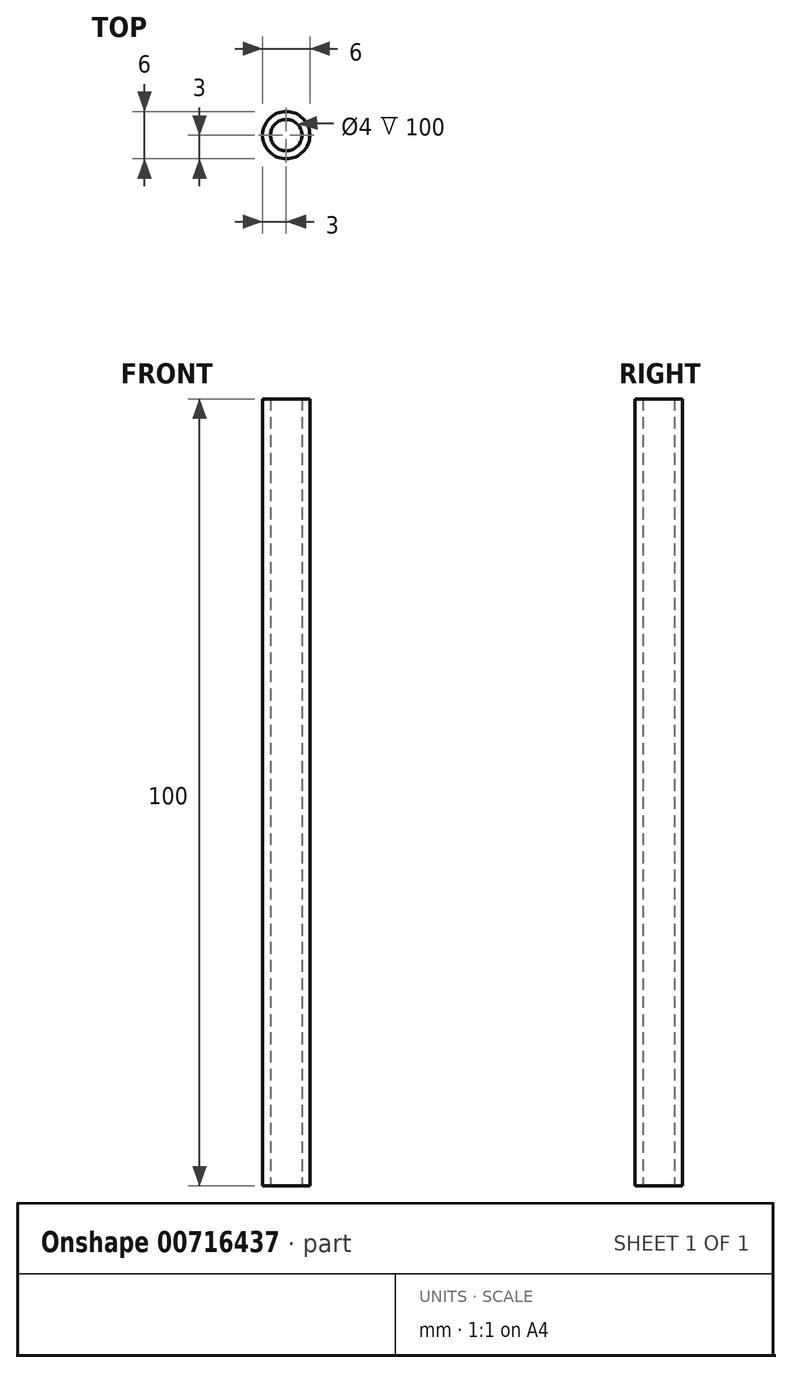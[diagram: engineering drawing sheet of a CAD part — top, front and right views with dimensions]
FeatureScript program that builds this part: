
annotation { "Feature Type Name" : "Feature", "Feature Type Description" : "" }
export const myFeature = defineFeature(function(context is Context, id is Id, definition is map)
    precondition{}
    {
        {
            var Q0;
            Q0=qCreatedBy(makeId("Top.planeOp"),FACE);
            var sketch = newSketch(context, id + "F0", { "sketchPlane" : qUnion([Q0])});
            skCircle(sketch, "E0", {"center": v(0, 0) * mm, "radius": 3 * mm});
            skCircle(sketch, "E1", {"center": v(0, 0) * mm, "radius": 2 * mm});
            skSolve(sketch);
        }
        {
            var Q0;
            Q0=qSketchRegion(id+"F0",true);
            extrude(context, id + "F1", {"entities" : qUnion([Q0]), "depth" : 100 * mm, "offsetDistance" : 25 * mm});
        }
    });
